FCSTD DOCUMENT  (FreeCAD 0.18R15340 (Git))
Label: default_pavement
License: All rights reserved
LicenseURL: http://en.wikipedia.org/wiki/All_rights_reserved
objects: Sketcher::SketchObject×1
note: 1 computed .brp shape members not serialized (recipe doc carries the construction recipe); baked Part::Feature solids carry a one-line shape summary decoded from their .brp

FEATURE [Sketcher::SketchObject] Sketch  label="Default_Pavement"
  expr: Constraints[9] = Constraints.width * 0.014999999999999999
  sketch-geometry (4):
    g0: LineSegment StartX=0 StartY=-5.45735e-11 StartZ=0 EndX=3657.6 EndY=-54.864 EndZ=0
    g1: LineSegment StartX=3657.6 StartY=-54.864 StartZ=0 EndX=3657.6 EndY=-359.664 EndZ=0
    g2: LineSegment StartX=3657.6 StartY=-359.664 StartZ=0 EndX=0 EndY=-304.801 EndZ=0
    g3: LineSegment StartX=0 StartY=-304.801 StartZ=0 EndX=0 EndY=-5.45697e-11 EndZ=0
  constraints (11):
    c: Coincident(g0,g1)
    c: Coincident(g1,g2)
    c: Coincident(g2,g3)
    c: Coincident(g3,g0)
    c: Vertical(g1)
    c: Vertical(g3)
    c: Coincident(g0,g-1)
    c: DistanceX(g0,g0) = 3657.6  'width'
    c: DistanceY(g1,g1) = 304.8
    c: DistanceY(g0,g0) = 54.864
    c: Parallel(g2,g0)
